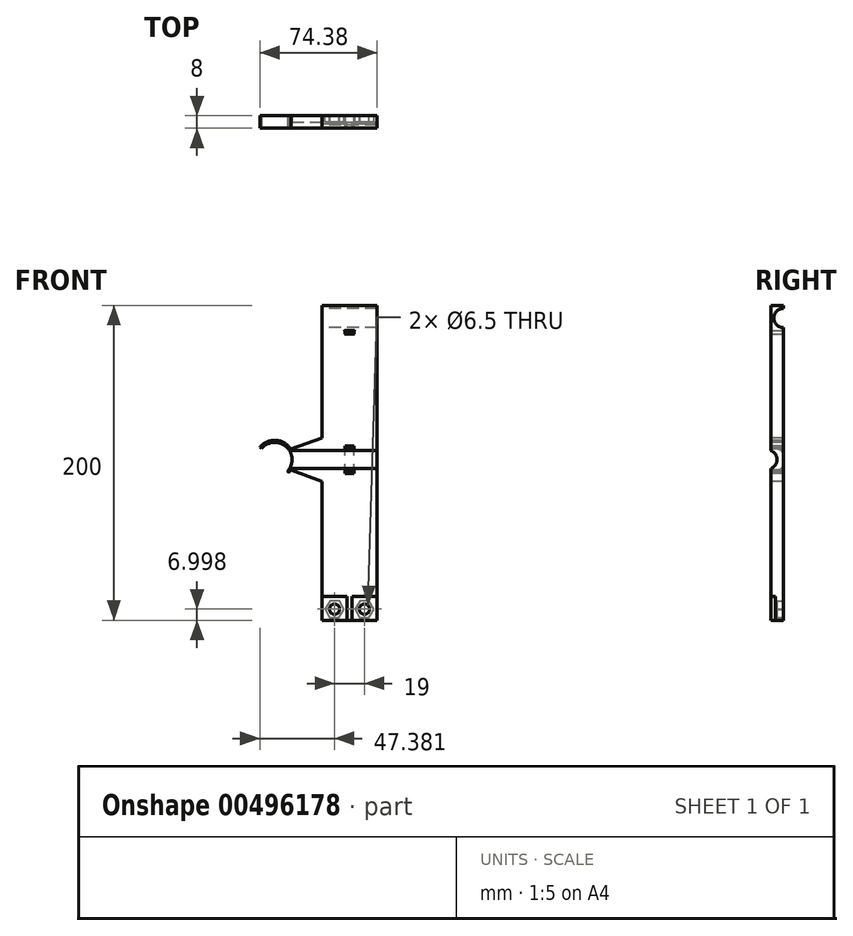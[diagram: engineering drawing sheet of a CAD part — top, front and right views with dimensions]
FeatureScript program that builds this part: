
annotation { "Feature Type Name" : "Feature", "Feature Type Description" : "" }
export const myFeature = defineFeature(function(context is Context, id is Id, definition is map)
    precondition{}
    {
        {
            var Q0;
            Q0=qCreatedBy(makeId("Front.planeOp"),FACE);
            var sketch = newSketch(context, id + "F0", { "sketchPlane" : qUnion([Q0])});
            skLineSegment(sketch, "E0.bottom", {"start": v(-13.38, 145.24) * mm, "end": v(21.62, 145.24) * mm});
            skLineSegment(sketch, "E0.top", {"start": v(-13.38, -54.76) * mm, "end": v(21.62, -54.76) * mm});
            skLineSegment(sketch, "E0.left", {"start": v(-13.38, 145.24) * mm, "end": v(-13.38, -54.76) * mm});
            skLineSegment(sketch, "E0.right", {"start": v(21.62, 145.24) * mm, "end": v(21.62, -54.76) * mm});
            skLineSegment(sketch, "E1", {"start": v(21.62, 145.24) * mm, "end": v(21.62, 137.24) * mm, "construction": true});
            skLineSegment(sketch, "E2", {"start": v(21.62, 137.24) * mm, "end": v(-13.38, 137.24) * mm, "construction": true});
            skSolve(sketch);
        }
        {
            var Q0;
            Q0=makeQuery(id+"F0.imprint","IMPRINT",FACE,{"disambiguationData":[TD([[makeQuery(id+"F0.imprint","IMPRINT",EDGE,{"derivedFrom":sQuery(id+"F0.wireOp",EDGE,"E0.bottom")}),-1.0]])]});
            extrude(context, id + "F1", {"entities" : qUnion([Q0]), "depth" : 8 * mm});
        }
        {
            var Q0;
            Q0=makeQuery(id+"F1.opExtrude","SWEPT_FACE",FACE,{"disambiguationData":[OSD([sQuery(id+"F0.wireOp",EDGE,"E0.left")])]});
            var sketch = newSketch(context, id + "F2", { "sketchPlane" : qUnion([Q0])});
            skLineSegment(sketch, "E3", {"start": v(0, 145.24) * mm, "end": v(0, 137.24) * mm, "construction": true});
            skLineSegment(sketch, "E4", {"start": v(0, 137.24) * mm, "end": v(-10.7, 137.24) * mm, "construction": true});
            skCircle(sketch, "E5", {"center": v(0, 137.24) * mm, "radius": 6.08 * mm, "construction": true});
            skCircle(sketch, "E6", {"center": v(0, 137.24) * mm, "radius": 6.08 * mm});
            skSolve(sketch);
        }
        {
            var Q0;
            Q0 = qSketchRegion(id + "F2", true);
            extrude(context, id + "F3", {"entities" : qUnion([Q0]), "operationType" : NewBodyOperationType.REMOVE, "oppositeDirection" : true, "depth" : 45 * mm});
        }
        {
            var Q0;
            {var subQ0=sQuery(id+"F0.wireOp",EDGE,"E0.top");var subQ1=sQuery(id+"F0.wireOp",EDGE,"E0.left");var subQ2=sQuery(id+"F0.wireOp",EDGE,"E0.right");Q0=makeQuery(id+"F3.boolean.opBoolean","SPLIT",FACE,{"disambiguationData":[TD([makeQuery(id+"F1.opExtrude","SWEPT_FACE",FACE,{"disambiguationData":[OSD([subQ0])]})])],"derivedFrom":makeQuery(id+"F1.opExtrude","CAP_FACE",FACE,{"disambiguationData":[OSD([sQuery(id+"F0.wireOp",EDGE,"E0.bottom"),subQ0,subQ1,subQ2])],"isStart":true})});}
            var sketch = newSketch(context, id + "F4", { "sketchPlane" : qUnion([Q0])});
            skLineSegment(sketch, "E7", {"start": v(-4.12, 129.16) * mm, "end": v(-1.12, 129.16) * mm, "construction": true});
            skLineSegment(sketch, "E8", {"start": v(-1.12, 129.16) * mm, "end": v(-7.12, 129.16) * mm, "construction": true});
            skLineSegment(sketch, "E9.bottom", {"start": v(-7.12, 129.16) * mm, "end": v(-1.12, 129.16) * mm});
            skLineSegment(sketch, "E9.top", {"start": v(-7.12, 127.16) * mm, "end": v(-1.12, 127.16) * mm});
            skLineSegment(sketch, "E9.left", {"start": v(-7.12, 129.16) * mm, "end": v(-7.12, 127.16) * mm});
            skLineSegment(sketch, "E9.right", {"start": v(-1.12, 129.16) * mm, "end": v(-1.12, 127.16) * mm});
            skSolve(sketch);
        }
        {
            var Q0;
            Q0=makeQuery(id+"F4.imprint","IMPRINT",FACE,{"disambiguationData":[TD([[makeQuery(id+"F4.imprint","IMPRINT",EDGE,{"derivedFrom":sQuery(id+"F4.wireOp",EDGE,"E9.bottom")}),-1.0]])]});
            var sketch = newSketch(context, id + "F5", { "sketchPlane" : qUnion([Q0])});
            skSolve(sketch);
        }
        {
            var Q0;
            Q0 = qSketchRegion(id + "F5", true);
            var Q1;
            Q1=makeQuery(id+"F4.imprint","IMPRINT",FACE,{"disambiguationData":[TD([[makeQuery(id+"F4.imprint","IMPRINT",EDGE,{"derivedFrom":sQuery(id+"F4.wireOp",EDGE,"E9.bottom")}),-1.0]])]});
            extrude(context, id + "F6", {"entities" : qUnion([Q0, Q1]), "operationType" : NewBodyOperationType.REMOVE, "oppositeDirection" : true, "depth" : 25 * mm});
        }
        {
            var Q0;
            Q0=makeQuery(id+"F6.boolean.opBoolean","INTERSECT",EDGE,{"derivedFrom":[makeQuery(id+"F1.opExtrude","CAP_FACE",FACE,{"disambiguationData":[OSD([sQuery(id+"F0.wireOp",EDGE,"E0.bottom"),sQuery(id+"F0.wireOp",EDGE,"E0.top"),sQuery(id+"F0.wireOp",EDGE,"E0.left"),sQuery(id+"F0.wireOp",EDGE,"E0.right")])],"isStart":false}),makeQuery(id+"F6.opExtrude","SWEPT_FACE",FACE,{"disambiguationData":[OSD([sQuery(id+"F4.wireOp",EDGE,"E9.bottom")])]})]});
            var Q1;
            Q1=makeQuery(id+"F6.boolean.opBoolean","INTERSECT",EDGE,{"derivedFrom":[makeQuery(id+"F1.opExtrude","CAP_FACE",FACE,{"disambiguationData":[OSD([sQuery(id+"F0.wireOp",EDGE,"E0.bottom"),sQuery(id+"F0.wireOp",EDGE,"E0.top"),sQuery(id+"F0.wireOp",EDGE,"E0.left"),sQuery(id+"F0.wireOp",EDGE,"E0.right")])],"isStart":false}),makeQuery(id+"F6.opExtrude","SWEPT_FACE",FACE,{"disambiguationData":[OSD([sQuery(id+"F4.wireOp",EDGE,"E9.top")])]})]});
            var Q2;
            Q2=makeQuery(id+"F6.boolean.opBoolean","INTERSECT",EDGE,{"derivedFrom":[makeQuery(id+"F1.opExtrude","CAP_FACE",FACE,{"disambiguationData":[OSD([sQuery(id+"F0.wireOp",EDGE,"E0.bottom"),sQuery(id+"F0.wireOp",EDGE,"E0.top"),sQuery(id+"F0.wireOp",EDGE,"E0.left"),sQuery(id+"F0.wireOp",EDGE,"E0.right")])],"isStart":false}),makeQuery(id+"F6.opExtrude","SWEPT_FACE",FACE,{"disambiguationData":[OSD([sQuery(id+"F4.wireOp",EDGE,"E9.left")])]})]});
            var Q3;
            Q3=makeQuery(id+"F6.boolean.opBoolean","INTERSECT",EDGE,{"derivedFrom":[makeQuery(id+"F1.opExtrude","CAP_FACE",FACE,{"disambiguationData":[OSD([sQuery(id+"F0.wireOp",EDGE,"E0.bottom"),sQuery(id+"F0.wireOp",EDGE,"E0.top"),sQuery(id+"F0.wireOp",EDGE,"E0.left"),sQuery(id+"F0.wireOp",EDGE,"E0.right")])],"isStart":false}),makeQuery(id+"F6.opExtrude","SWEPT_FACE",FACE,{"disambiguationData":[OSD([sQuery(id+"F4.wireOp",EDGE,"E9.right")])]})]});
            var Q4;
            Q4=makeQuery(id+"F6.boolean.opBoolean","COPY",EDGE,{"derivedFrom":makeQuery(id+"F6.opExtrude","CAP_EDGE",EDGE,{"disambiguationData":[OSD([sQuery(id+"F4.wireOp",EDGE,"E9.bottom")])],"isStart":true})});
            var Q5;
            Q5=makeQuery(id+"F6.boolean.opBoolean","COPY",EDGE,{"derivedFrom":makeQuery(id+"F6.opExtrude","CAP_EDGE",EDGE,{"disambiguationData":[OSD([sQuery(id+"F4.wireOp",EDGE,"E9.left")])],"isStart":true})});
            var Q6;
            Q6=makeQuery(id+"F6.boolean.opBoolean","COPY",EDGE,{"derivedFrom":makeQuery(id+"F6.opExtrude","CAP_EDGE",EDGE,{"disambiguationData":[OSD([sQuery(id+"F4.wireOp",EDGE,"E9.top")])],"isStart":true})});
            var Q7;
            Q7=makeQuery(id+"F6.boolean.opBoolean","COPY",EDGE,{"derivedFrom":makeQuery(id+"F6.opExtrude","CAP_EDGE",EDGE,{"disambiguationData":[OSD([sQuery(id+"F4.wireOp",EDGE,"E9.right")])],"isStart":true})});
            fillet(context, id + "F7", {"entities" : qUnion([Q0, Q1, Q2, Q3, Q4, Q5, Q6, Q7]), "radius" : 0.3 * mm, "tangentPropagation" : true, "allowEdgeOverflow" : false});
        }
        {
            var Q0;
            Q0=makeQuery(id+"F1.opExtrude","CAP_FACE",FACE,{"disambiguationData":[OSD([sQuery(id+"F0.wireOp",EDGE,"E0.bottom"),sQuery(id+"F0.wireOp",EDGE,"E0.top"),sQuery(id+"F0.wireOp",EDGE,"E0.left"),sQuery(id+"F0.wireOp",EDGE,"E0.right")])],"isStart":false});
            var sketch = newSketch(context, id + "F8", { "sketchPlane" : qUnion([Q0])});
            skLineSegment(sketch, "E10", {"start": v(-13.38, 145.24) * mm, "end": v(-13.38, -47.76) * mm, "construction": true});
            skLineSegment(sketch, "E11", {"start": v(-13.38, -47.76) * mm, "end": v(82.12, -47.76) * mm, "construction": true});
            skLineSegment(sketch, "E12", {"start": v(-13.38, -47.76) * mm, "end": v(21.62, -47.76) * mm, "construction": true});
            skLineSegment(sketch, "E13", {"start": v(21.62, -47.76) * mm, "end": v(13.62, -47.76) * mm, "construction": true});
            skLineSegment(sketch, "E14", {"start": v(13.62, -47.76) * mm, "end": v(13.62, -34.39) * mm, "construction": true});
            skLineSegment(sketch, "E15", {"start": v(-13.38, -47.76) * mm, "end": v(-5.38, -47.76) * mm, "construction": true});
            skLineSegment(sketch, "E16", {"start": v(-5.38, -43.12) * mm, "end": v(-5.38, -47.76) * mm, "construction": true});
            skCircle(sketch, "E17", {"center": v(-5.38, -47.76) * mm, "radius": 3.25 * mm});
            skCircle(sketch, "E18", {"center": v(13.62, -47.76) * mm, "radius": 3.25 * mm});
            skSolve(sketch);
        }
        {
            var Q0;
            Q0 = qSketchRegion(id + "F8", true);
            extrude(context, id + "F9", {"entities" : qUnion([Q0]), "operationType" : NewBodyOperationType.REMOVE, "oppositeDirection" : true, "depth" : 25 * mm});
        }
        {
            var Q0;
            {var subQ0=sQuery(id+"F0.wireOp",EDGE,"E0.top");var subQ1=sQuery(id+"F0.wireOp",EDGE,"E0.left");var subQ2=sQuery(id+"F0.wireOp",EDGE,"E0.right");Q0=makeQuery(id+"F3.boolean.opBoolean","SPLIT",FACE,{"disambiguationData":[TD([makeQuery(id+"F1.opExtrude","SWEPT_FACE",FACE,{"disambiguationData":[OSD([subQ0])]})])],"derivedFrom":makeQuery(id+"F1.opExtrude","CAP_FACE",FACE,{"disambiguationData":[OSD([sQuery(id+"F0.wireOp",EDGE,"E0.bottom"),subQ0,subQ1,subQ2])],"isStart":true})});}
            var sketch = newSketch(context, id + "F10", { "sketchPlane" : qUnion([Q0])});
            skLineSegment(sketch, "E19.bottom", {"start": v(13.38, -54.76) * mm, "end": v(30.88, -54.76) * mm});
            skLineSegment(sketch, "E19.top", {"start": v(13.38, -40.76) * mm, "end": v(30.88, -40.76) * mm});
            skLineSegment(sketch, "E19.left", {"start": v(13.38, -54.76) * mm, "end": v(13.38, -40.76) * mm});
            skLineSegment(sketch, "E19.right", {"start": v(30.88, -54.76) * mm, "end": v(30.88, -40.76) * mm});
            skCircle(sketch, "E20", {"center": v(5.38, -47.76) * mm, "radius": 6 * mm});
            skCircle(sketch, "E21.cCircle", {"center": v(5.38, -47.76) * mm, "radius": 6 * mm, "construction": true});
            skLineSegment(sketch, "E21.0", {"start": v(2.34, -42.59) * mm, "end": v(8.34, -42.54) * mm});
            skLineSegment(sketch, "E21.1", {"start": v(8.34, -42.54) * mm, "end": v(11.38, -47.71) * mm});
            skLineSegment(sketch, "E21.2", {"start": v(11.38, -47.71) * mm, "end": v(8.42, -52.93) * mm});
            skLineSegment(sketch, "E21.3", {"start": v(8.42, -52.93) * mm, "end": v(2.42, -52.98) * mm});
            skLineSegment(sketch, "E21.4", {"start": v(2.42, -52.98) * mm, "end": v(-0.62, -47.8) * mm});
            skLineSegment(sketch, "E21.5", {"start": v(-0.62, -47.8) * mm, "end": v(2.34, -42.59) * mm});
            skCircle(sketch, "E22", {"center": v(-13.62, -47.76) * mm, "radius": 6 * mm});
            skCircle(sketch, "E23.cCircle", {"center": v(-13.62, -47.76) * mm, "radius": 6 * mm, "construction": true});
            skLineSegment(sketch, "E23.0", {"start": v(-10.6, -52.94) * mm, "end": v(-16.6, -52.97) * mm});
            skLineSegment(sketch, "E23.1", {"start": v(-16.6, -52.97) * mm, "end": v(-19.62, -47.8) * mm});
            skLineSegment(sketch, "E23.2", {"start": v(-19.62, -47.8) * mm, "end": v(-16.65, -42.58) * mm});
            skLineSegment(sketch, "E23.3", {"start": v(-16.65, -42.58) * mm, "end": v(-10.65, -42.55) * mm});
            skLineSegment(sketch, "E23.4", {"start": v(-10.65, -42.55) * mm, "end": v(-7.62, -47.73) * mm});
            skLineSegment(sketch, "E23.5", {"start": v(-7.62, -47.73) * mm, "end": v(-10.6, -52.94) * mm});
            skSolve(sketch);
        }
        {
            var Q0;
            Q0=makeQuery(id+"F10.imprint","IMPRINT",FACE,{"disambiguationData":[TD([[makeQuery(id+"F10.imprint","IMPRINT",EDGE,{"derivedFrom":sQuery(id+"F10.wireOp",EDGE,"E23.0")}),-1.0]])]});
            var Q1;
            Q1=makeQuery(id+"F10.imprint","IMPRINT",FACE,{"disambiguationData":[TD([[makeQuery(id+"F10.imprint","IMPRINT",EDGE,{"derivedFrom":sQuery(id+"F10.wireOp",EDGE,"E21.0")}),-1.0]])]});
            extrude(context, id + "F11", {"entities" : qUnion([Q0, Q1]), "operationType" : NewBodyOperationType.REMOVE, "oppositeDirection" : true, "depth" : 4 * mm});
        }
        {
            var Q0;
            Q0=makeQuery(id+"F1.opExtrude","CAP_FACE",FACE,{"disambiguationData":[OSD([sQuery(id+"F0.wireOp",EDGE,"E0.bottom"),sQuery(id+"F0.wireOp",EDGE,"E0.top"),sQuery(id+"F0.wireOp",EDGE,"E0.left"),sQuery(id+"F0.wireOp",EDGE,"E0.right")])],"isStart":false});
            var sketch = newSketch(context, id + "F12", { "sketchPlane" : qUnion([Q0])});
            skLineSegment(sketch, "E24.bottom", {"start": v(-13.38, -54.76) * mm, "end": v(21.62, -54.76) * mm});
            skLineSegment(sketch, "E24.left", {"start": v(-13.38, -54.76) * mm, "end": v(-13.38, -40.6) * mm});
            skLineSegment(sketch, "E24.right", {"start": v(21.62, -54.76) * mm, "end": v(21.62, -40.6) * mm});
            skLineSegment(sketch, "E25.top", {"start": v(-13.38, -39.76) * mm, "end": v(21.62, -39.76) * mm});
            skLineSegment(sketch, "E25.left", {"start": v(-13.38, -54.76) * mm, "end": v(-13.38, -39.76) * mm});
            skLineSegment(sketch, "E25.right", {"start": v(21.62, -54.76) * mm, "end": v(21.62, -39.76) * mm});
            skSolve(sketch);
        }
        {
            var Q0;
            Q0 = qSketchRegion(id + "F12", true);
            var Q1;
            Q1=makeQuery(id+"F12.imprint","IMPRINT",FACE,{"disambiguationData":[TD([[makeQuery(id+"F12.imprint","IMPRINT",EDGE,{"derivedFrom":sQuery(id+"F12.wireOp",EDGE,"E24.bottom")}),1.0]])]});
            extrude(context, id + "F13", {"entities" : qUnion([Q0, Q1]), "operationType" : NewBodyOperationType.REMOVE, "oppositeDirection" : true, "depth" : 3 * mm});
        }
        {
            var Q0;
            Q0=makeQuery(id+"F13.boolean.opBoolean","COPY",FACE,{"derivedFrom":makeQuery(id+"F13.opExtrude","CAP_FACE",FACE,{"disambiguationData":[OSD([sQuery(id+"F12.wireOp",EDGE,"E24.bottom"),sQuery(id+"F12.wireOp",EDGE,"E25.top"),sQuery(id+"F12.wireOp",EDGE,"E25.left"),sQuery(id+"F12.wireOp",EDGE,"E25.right")])],"isStart":false})});
            var sketch = newSketch(context, id + "F14", { "sketchPlane" : qUnion([Q0])});
            skLineSegment(sketch, "E26", {"start": v(-13.38, -54.76) * mm, "end": v(2.62, -54.76) * mm, "construction": true});
            skLineSegment(sketch, "E27.bottom", {"start": v(2.62, -54.76) * mm, "end": v(5.62, -54.76) * mm});
            skLineSegment(sketch, "E27.top", {"start": v(2.62, -39.76) * mm, "end": v(5.62, -39.76) * mm});
            skLineSegment(sketch, "E27.left", {"start": v(2.62, -54.76) * mm, "end": v(2.62, -39.76) * mm});
            skLineSegment(sketch, "E27.right", {"start": v(5.62, -54.76) * mm, "end": v(5.62, -39.76) * mm});
            skSolve(sketch);
        }
        {
            var Q0;
            Q0=makeQuery(id+"F14.imprint","IMPRINT",FACE,{"disambiguationData":[TD([[makeQuery(id+"F14.imprint","IMPRINT",EDGE,{"derivedFrom":sQuery(id+"F14.wireOp",EDGE,"E27.bottom")}),1.0]])]});
            extrude(context, id + "F15", {"entities" : qUnion([Q0]), "operationType" : NewBodyOperationType.ADD, "depth" : 3 * mm});
        }
        {
            var Q0;
            Q0=makeQuery(id+"F15.boolean.opBoolean","MERGE",FACE,{"derivedFrom":[makeQuery(id+"F1.opExtrude","CAP_FACE",FACE,{"disambiguationData":[OSD([sQuery(id+"F0.wireOp",EDGE,"E0.bottom"),sQuery(id+"F0.wireOp",EDGE,"E0.top"),sQuery(id+"F0.wireOp",EDGE,"E0.left"),sQuery(id+"F0.wireOp",EDGE,"E0.right")])],"isStart":false}),makeQuery(id+"F15.opExtrude","CAP_FACE",FACE,{"disambiguationData":[OSD([sQuery(id+"F14.wireOp",EDGE,"E27.bottom"),sQuery(id+"F14.wireOp",EDGE,"E27.top"),sQuery(id+"F14.wireOp",EDGE,"E27.left"),sQuery(id+"F14.wireOp",EDGE,"E27.right")])],"isStart":false})]});
            var sketch = newSketch(context, id + "F16", { "sketchPlane" : qUnion([Q0])});
            skLineSegment(sketch, "E28", {"start": v(-51.18, 47.24) * mm, "end": v(-13.38, 47.24) * mm, "construction": true});
            skLineSegment(sketch, "E29", {"start": v(-13.38, 47.24) * mm, "end": v(-43.38, 47.24) * mm, "construction": true});
            skLineSegment(sketch, "E30", {"start": v(-43.38, 47.24) * mm, "end": v(-43.38, 58.24) * mm, "construction": true});
            skArc(sketch, "E31", {"start": v(-35.16, 39.93) * mm, "mid": v(-36.21, 55.58) * mm, "end": v(-51.85, 54.26) * mm, "construction": true});
            skArc(sketch, "E32.0", {"start": v(-34.25, 39.15) * mm, "mid": v(-33.66, 39.87) * mm, "end": v(-33.13, 40.63) * mm});
            skLineSegment(sketch, "E33", {"start": v(-33.13, 40.63) * mm, "end": v(-13.38, 33.4) * mm});
            skLineSegment(sketch, "E34", {"start": v(-13.38, 33.4) * mm, "end": v(-13.38, 68.13) * mm});
            skArc(sketch, "E35", {"start": v(-35.16, 39.93) * mm, "mid": v(-36.21, 55.58) * mm, "end": v(-51.85, 54.26) * mm});
            skLineSegment(sketch, "E36.MirrorCS", {"start": v(-33.13, 53.85) * mm, "end": v(-13.38, 61.08) * mm});
            skLineSegment(sketch, "E37", {"start": v(-34.25, 39.15) * mm, "end": v(-35.16, 39.93) * mm});
            skArc(sketch, "E38.trimOffspring", {"start": v(-33.13, 53.85) * mm, "mid": v(-42.64, 59.42) * mm, "end": v(-52.76, 55.04) * mm});
            skLineSegment(sketch, "E39.trimOffspring", {"start": v(-51.85, 54.26) * mm, "end": v(-52.76, 55.04) * mm});
            skLineSegment(sketch, "E40", {"start": v(-13.38, 145.24) * mm, "end": v(-13.38, 47.24) * mm, "construction": true});
            skLineSegment(sketch, "E41", {"start": v(-13.38, 47.24) * mm, "end": v(51.67, 47.24) * mm, "construction": true});
            skSolve(sketch);
        }
        {
            var Q0;
            {var subQ4=sQuery(id+"F0.wireOp",EDGE,"E0.bottom");var subQ12=makeQuery(id+"F1.opExtrude","CAP_EDGE",EDGE,{"disambiguationData":[OSD([subQ4])],"isStart":false});Q0=makeQuery(id+"F16.imprint","IMPRINT",FACE,{"disambiguationData":[TD([[makeQuery(id+"F16.imprint","IMPRINT",EDGE,{"derivedFrom":subQ12}),-1.0]])]});}
            var sketch = newSketch(context, id + "F17", { "sketchPlane" : qUnion([Q0])});
            skLineSegment(sketch, "E42", {"start": v(-13.38, 145.24) * mm, "end": v(-13.38, 47.24) * mm, "construction": true});
            skSolve(sketch);
        }
        {
            var Q0;
            Q0=makeQuery(id+"F16.imprint","IMPRINT",FACE,{"disambiguationData":[TD([[makeQuery(id+"F16.imprint","IMPRINT",EDGE,{"derivedFrom":sQuery(id+"F16.wireOp",EDGE,"E32.0")}),1.0]])]});
            extrude(context, id + "F18", {"entities" : qUnion([Q0]), "operationType" : NewBodyOperationType.ADD, "oppositeDirection" : true, "depth" : 8 * mm});
        }
        {
            var Q0;
            Q0=makeQuery(id+"F1.opExtrude","SWEPT_FACE",FACE,{"disambiguationData":[OSD([sQuery(id+"F0.wireOp",EDGE,"E0.right")])]});
            var sketch = newSketch(context, id + "F19", { "sketchPlane" : qUnion([Q0])});
            skLineSegment(sketch, "E43", {"start": v(-10, 47.24) * mm, "end": v(-3.26, 47.02) * mm, "construction": true});
            skCircle(sketch, "E44", {"center": v(-10, 47.24) * mm, "radius": 6 * mm});
            skSolve(sketch);
        }
        {
            var Q0;
            {var subQ0=sQuery(id+"F19.wireOp",EDGE,"E44");var subQ1=makeQuery(id+"F1.opExtrude","CAP_EDGE",EDGE,{"disambiguationData":[OSD([sQuery(id+"F0.wireOp",EDGE,"E0.right")])],"isStart":false});var subQ2=makeQuery(id+"F19.imprint","INTERSECT",VERTEX,{"disambiguationData":[OD(0.0)],"derivedFrom":[subQ1,subQ0]});Q0=makeQuery(id+"F19.imprint","IMPRINT",FACE,{"disambiguationData":[TD([[makeQuery(id+"F19.imprint","IMPRINT",EDGE,{"disambiguationData":[TD([[subQ2,1.0]])],"derivedFrom":subQ0}),1.0]])]});}
            extrude(context, id + "F20", {"entities" : qUnion([Q0]), "operationType" : NewBodyOperationType.REMOVE, "oppositeDirection" : true, "depth" : 65 * mm});
        }
        {
            var Q0;
            {var subQ4=sQuery(id+"F0.wireOp",EDGE,"E0.bottom");var subQ12=makeQuery(id+"F1.opExtrude","CAP_EDGE",EDGE,{"disambiguationData":[OSD([subQ4])],"isStart":false});Q0=makeQuery(id+"F17.imprint","IMPRINT",FACE,{"disambiguationData":[TD([[makeQuery(id+"F17.imprint","IMPRINT",EDGE,{"derivedFrom":makeQuery(id+"F16.imprint","IMPRINT",EDGE,{"derivedFrom":subQ12})}),-1.0]])]});}
            var sketch = newSketch(context, id + "F21", { "sketchPlane" : qUnion([Q0])});
            skLineSegment(sketch, "E45.bottom", {"start": v(7.12, 38.59) * mm, "end": v(1.12, 38.59) * mm});
            skLineSegment(sketch, "E45.top", {"start": v(7.12, 40.59) * mm, "end": v(1.12, 40.59) * mm});
            skLineSegment(sketch, "E45.left", {"start": v(7.12, 38.59) * mm, "end": v(7.12, 40.59) * mm});
            skLineSegment(sketch, "E45.right", {"start": v(1.12, 38.59) * mm, "end": v(1.12, 40.59) * mm});
            skLineSegment(sketch, "E46.bottom", {"start": v(7.12, 53.9) * mm, "end": v(1.12, 53.9) * mm});
            skLineSegment(sketch, "E46.top", {"start": v(7.12, 55.9) * mm, "end": v(1.12, 55.9) * mm});
            skLineSegment(sketch, "E46.left", {"start": v(7.12, 53.9) * mm, "end": v(7.12, 55.9) * mm});
            skLineSegment(sketch, "E46.right", {"start": v(1.12, 53.9) * mm, "end": v(1.12, 55.9) * mm});
            skSolve(sketch);
        }
        {
            var Q0;
            Q0 = qSketchRegion(id + "F21", true);
            extrude(context, id + "F22", {"entities" : qUnion([Q0]), "operationType" : NewBodyOperationType.REMOVE, "oppositeDirection" : true, "depth" : 25 * mm});
        }
        {
            var Q0;
            {var subQ0=sQuery(id+"F0.wireOp",EDGE,"E0.top");var subQ1=sQuery(id+"F0.wireOp",EDGE,"E0.left");var subQ2=sQuery(id+"F0.wireOp",EDGE,"E0.right");Q0=makeQuery(id+"F22.boolean.opBoolean","INTERSECT",EDGE,{"derivedFrom":[makeQuery(id+"F18.boolean.opBoolean","MERGE",FACE,{"derivedFrom":[makeQuery(id+"F3.boolean.opBoolean","SPLIT",FACE,{"disambiguationData":[TD([makeQuery(id+"F1.opExtrude","SWEPT_FACE",FACE,{"disambiguationData":[OSD([subQ0])]})])],"derivedFrom":makeQuery(id+"F1.opExtrude","CAP_FACE",FACE,{"disambiguationData":[OSD([sQuery(id+"F0.wireOp",EDGE,"E0.bottom"),subQ0,subQ1,subQ2])],"isStart":true})}),makeQuery(id+"F18.opExtrude","CAP_FACE",FACE,{"disambiguationData":[OSD([sQuery(id+"F16.wireOp",EDGE,"E32.0"),sQuery(id+"F16.wireOp",EDGE,"E33"),sQuery(id+"F16.wireOp",EDGE,"E34"),sQuery(id+"F16.wireOp",EDGE,"E35"),sQuery(id+"F16.wireOp",EDGE,"E36.MirrorCS"),sQuery(id+"F16.wireOp",EDGE,"E37"),sQuery(id+"F16.wireOp",EDGE,"E38.trimOffspring"),sQuery(id+"F16.wireOp",EDGE,"E39.trimOffspring")])],"isStart":false})]}),makeQuery(id+"F22.opExtrude","SWEPT_FACE",FACE,{"disambiguationData":[OSD([sQuery(id+"F21.wireOp",EDGE,"E45.top")])]})]});}
            var Q1;
            {var subQ0=sQuery(id+"F0.wireOp",EDGE,"E0.top");var subQ1=sQuery(id+"F0.wireOp",EDGE,"E0.left");var subQ2=sQuery(id+"F0.wireOp",EDGE,"E0.right");Q1=makeQuery(id+"F22.boolean.opBoolean","INTERSECT",EDGE,{"derivedFrom":[makeQuery(id+"F18.boolean.opBoolean","MERGE",FACE,{"derivedFrom":[makeQuery(id+"F3.boolean.opBoolean","SPLIT",FACE,{"disambiguationData":[TD([makeQuery(id+"F1.opExtrude","SWEPT_FACE",FACE,{"disambiguationData":[OSD([subQ0])]})])],"derivedFrom":makeQuery(id+"F1.opExtrude","CAP_FACE",FACE,{"disambiguationData":[OSD([sQuery(id+"F0.wireOp",EDGE,"E0.bottom"),subQ0,subQ1,subQ2])],"isStart":true})}),makeQuery(id+"F18.opExtrude","CAP_FACE",FACE,{"disambiguationData":[OSD([sQuery(id+"F16.wireOp",EDGE,"E32.0"),sQuery(id+"F16.wireOp",EDGE,"E33"),sQuery(id+"F16.wireOp",EDGE,"E34"),sQuery(id+"F16.wireOp",EDGE,"E35"),sQuery(id+"F16.wireOp",EDGE,"E36.MirrorCS"),sQuery(id+"F16.wireOp",EDGE,"E37"),sQuery(id+"F16.wireOp",EDGE,"E38.trimOffspring"),sQuery(id+"F16.wireOp",EDGE,"E39.trimOffspring")])],"isStart":false})]}),makeQuery(id+"F22.opExtrude","SWEPT_FACE",FACE,{"disambiguationData":[OSD([sQuery(id+"F21.wireOp",EDGE,"E46.bottom")])]})]});}
            fillet(context, id + "F23", {"entities" : qUnion([Q0, Q1]), "radius" : 4 * mm, "tangentPropagation" : true, "allowEdgeOverflow" : false});
        }
    });
